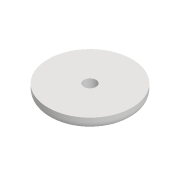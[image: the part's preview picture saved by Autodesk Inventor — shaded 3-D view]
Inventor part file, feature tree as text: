
AUTODESK INVENTOR PART (.ipt)
format: ipt  version: 2022 (Build 260153000, 153)  size: 108,032 bytes
history: native  units: mm
features: extrude x1, fillet x1, sketch x1
ambient origin geometry x8: Origin, YZ Plane, XZ Plane, XY Plane, X Axis, Y Axis, Z Axis, Center Point
bodies: Solid1 (feature_tree)
feature tree (3):
  extrude  "Extrusion1"  Depth=2.0mm
  fillet  "Fillet1"  Radius=3.0mm
  sketch  "Sketch1"  dims[d0=22.0mm d1=3.2mm d2=3.0mm d3=0.0mm d4=2.0mm]
